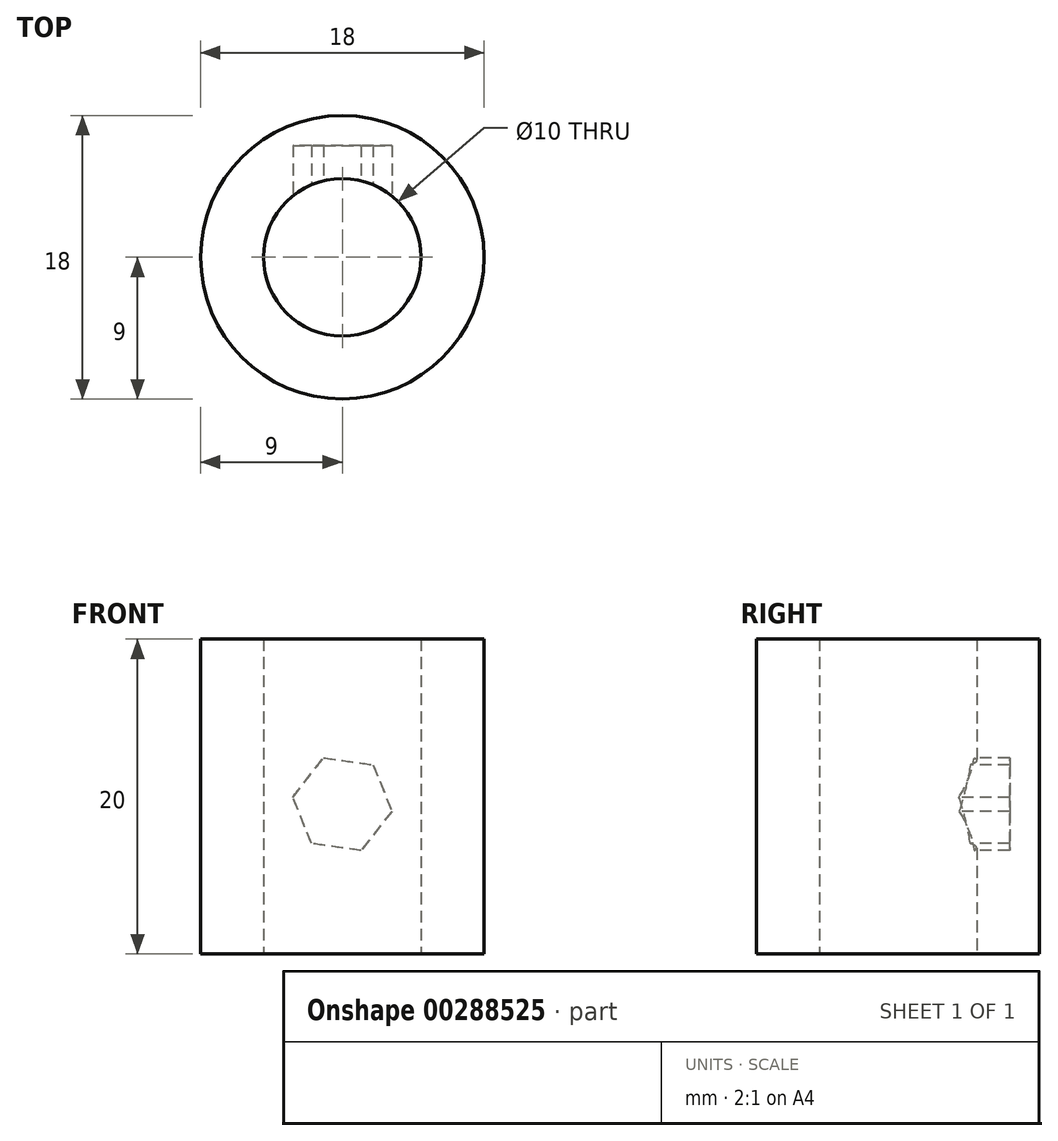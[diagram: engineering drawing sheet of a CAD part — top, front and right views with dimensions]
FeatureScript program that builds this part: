
annotation { "Feature Type Name" : "Feature", "Feature Type Description" : "" }
export const myFeature = defineFeature(function(context is Context, id is Id, definition is map)
    precondition{}
    {
        {
            var Q0;
            Q0=qCreatedBy(makeId("Top.planeOp"),FACE);
            var sketch = newSketch(context, id + "F0", { "sketchPlane" : qUnion([Q0])});
            skCircle(sketch, "E0", {"center": v(0, 0) * mm, "radius": 5 * mm});
            skCircle(sketch, "E1", {"center": v(0, 0) * mm, "radius": 9 * mm});
            skSolve(sketch);
        }
        {
            var Q0;
            Q0 = qSketchRegion(id + "F0", true);
            extrude(context, id + "F1", {"entities" : qUnion([Q0]), "depth" : 20 * mm});
        }
        {
            var Q0;
            Q0=qCreatedBy(makeId("Front.planeOp"),FACE);
            var sketch = newSketch(context, id + "F2", { "sketchPlane" : qUnion([Q0])});
            skCircle(sketch, "E2", {"center": v(0, 9.51) * mm, "radius": 2.75 * mm, "construction": true});
            skLineSegment(sketch, "E3.0", {"start": v(-3.14, 9.96) * mm, "end": v(-1.19, 12.46) * mm});
            skLineSegment(sketch, "E3.1", {"start": v(-1.19, 12.46) * mm, "end": v(1.96, 12.01) * mm});
            skLineSegment(sketch, "E3.2", {"start": v(1.96, 12.01) * mm, "end": v(3.14, 9.07) * mm});
            skLineSegment(sketch, "E3.3", {"start": v(3.14, 9.07) * mm, "end": v(1.19, 6.57) * mm});
            skLineSegment(sketch, "E3.4", {"start": v(1.19, 6.57) * mm, "end": v(-1.96, 7.01) * mm});
            skLineSegment(sketch, "E3.5", {"start": v(-1.96, 7.01) * mm, "end": v(-3.14, 9.96) * mm});
            skPoint(sketch, "E3.0.midPoint", {"position": v(-2.17, 11.2) * mm});
            skCircle(sketch, "E4", {"center": v(0, 9.51) * mm, "radius": 1.6 * mm});
            skSolve(sketch);
        }
        {
            var Q0;
            Q0=makeQuery(id+"F2.imprint","IMPRINT",FACE,{"disambiguationData":[TD([[makeQuery(id+"F2.imprint","IMPRINT",EDGE,{"derivedFrom":sQuery(id+"F2.wireOp",EDGE,"E3.0")}),-1.0]])]});
            var Q1;
            Q1=makeQuery(id+"F2.imprint","IMPRINT",FACE,{"disambiguationData":[TD([[makeQuery(id+"F2.imprint","IMPRINT",EDGE,{"derivedFrom":sQuery(id+"F2.wireOp",EDGE,"E4")}),1.0]])]});
            extrude(context, id + "F3", {"entities" : qUnion([Q0, Q1]), "operationType" : NewBodyOperationType.REMOVE, "oppositeDirection" : true, "depth" : 7.1 * mm});
        }
    });
